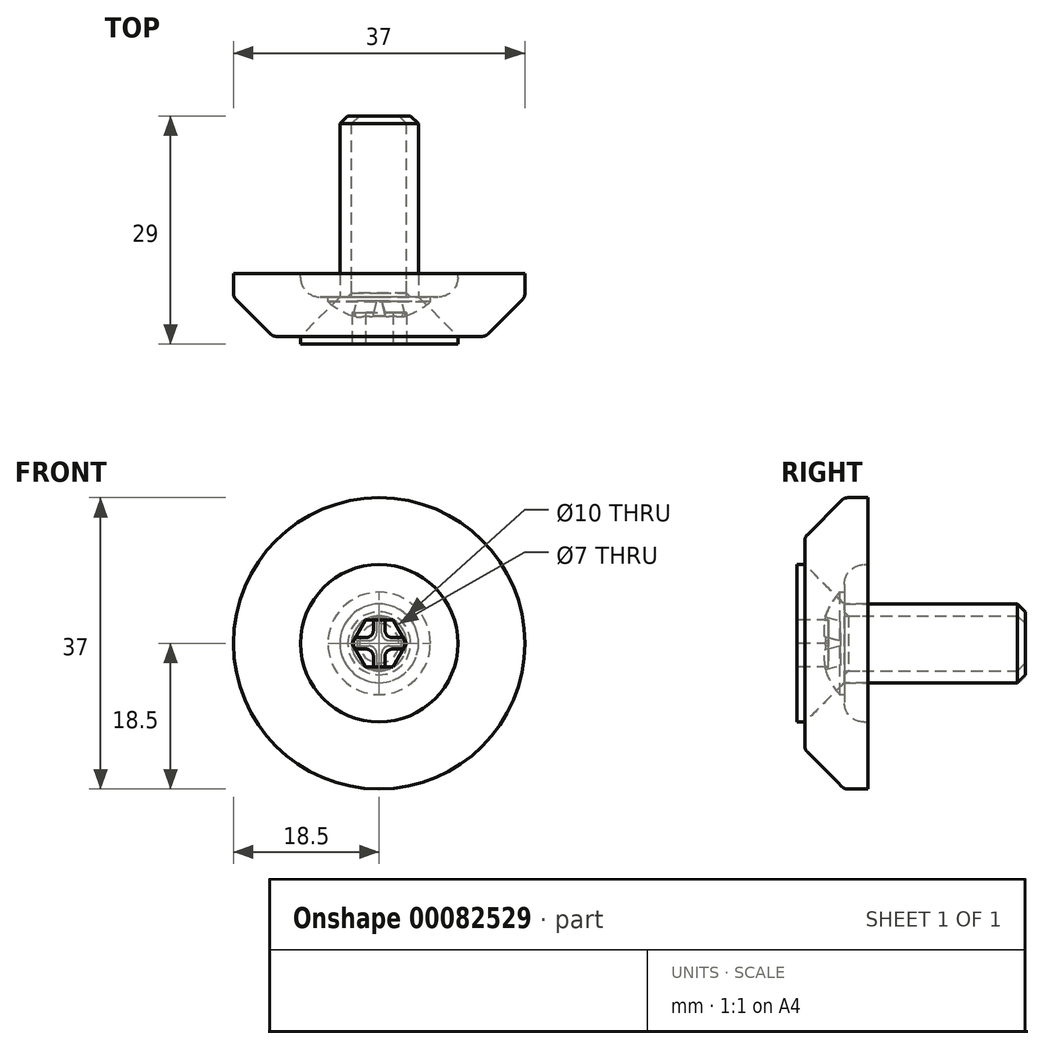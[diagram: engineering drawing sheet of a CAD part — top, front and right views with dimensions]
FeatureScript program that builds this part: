
annotation { "Feature Type Name" : "Feature", "Feature Type Description" : "" }
export const myFeature = defineFeature(function(context is Context, id is Id, definition is map)
    precondition{}
    {
        {
            var Q0;
            Q0=qCreatedBy(makeId("Top.planeOp"),FACE);
            var sketch = newSketch(context, id + "F0", { "sketchPlane" : qUnion([Q0])});
            skLineSegment(sketch, "E0", {"start": v(0, 0) * mm, "end": v(0, 50) * mm, "construction": true});
            skSolve(sketch);
        }
        {
            var Q0;
            Q0=qCreatedBy(makeId("Front.planeOp"),FACE);
            var sketch = newSketch(context, id + "F1", { "sketchPlane" : qUnion([Q0])});
            skLineSegment(sketch, "E1", {"start": v(0, 0) * mm, "end": v(0, 50) * mm, "construction": true});
            skSolve(sketch);
        }
        {
            var Q0;
            Q0=qCreatedBy(makeId("Right.planeOp"),FACE);
            var sketch = newSketch(context, id + "F2", { "sketchPlane" : qUnion([Q0])});
            skLineSegment(sketch, "E2.0", {"start": v(0, 0) * mm, "end": v(50, 0) * mm, "construction": true});
            skLineSegment(sketch, "E3", {"start": v(0, 0) * mm, "end": v(0, 10) * mm});
            skLineSegment(sketch, "E4", {"start": v(0, 10) * mm, "end": v(-0.5, 10) * mm});
            skLineSegment(sketch, "E5", {"start": v(0, 0) * mm, "end": v(-3, 0) * mm});
            skArc(sketch, "E6", {"start": v(-0.5, 10) * mm, "mid": v(-2.27, 9.27) * mm, "end": v(-3, 7.5) * mm});
            skLineSegment(sketch, "E7", {"start": v(-3, 7.5) * mm, "end": v(-3, 0) * mm});
            skSolve(sketch);
        }
        {
            var Q0;
            Q0=makeQuery(id+"F2.imprint","IMPRINT",FACE,{"disambiguationData":[TD([[makeQuery(id+"F2.imprint","IMPRINT",EDGE,{"derivedFrom":sQuery(id+"F2.wireOp",EDGE,"E3")}),1.0]])]});
            var Q1;
            Q1=sQuery(id+"F2.wireOp",EDGE,"E5");
            revolve(context, id + "F3", {"entities" : qUnion([Q0]), "axis" : qUnion([Q1]), "revolveType" : RevolveType.FULL});
        }
        {
            var Q0;
            Q0=makeQuery(id+"F3.opRevolve","SWEPT_FACE",FACE,{"disambiguationData":[OSD([sQuery(id+"F2.wireOp",EDGE,"E7")])]});
            var sketch = newSketch(context, id + "F4", { "sketchPlane" : qUnion([Q0])});
            skPoint(sketch, "E8", {"position": v(0, 0) * mm});
            skSolve(sketch);
        }
        {
            var Q0;
            Q0=sQuery(id+"F4.wireOp",VERTEX,"E8");
            var Q1;
            Q1=makeQuery(id+"F3.opRevolve","SWEPT_BODY",BODY,{"disambiguationData":[OSD([sQuery(id+"F2.wireOp",EDGE,"E3"),sQuery(id+"F2.wireOp",EDGE,"E4"),sQuery(id+"F2.wireOp",EDGE,"E5"),sQuery(id+"F2.wireOp",EDGE,"E6"),sQuery(id+"F2.wireOp",EDGE,"E7")])]});
            hole(context, id + "F5", {"style" : HoleStyle.C_SINK, "endStyle" : HoleEndStyle.THROUGH, "holeDiameter" : 7 * mm, "cSinkDiameter" : 8 * mm, "cSinkAngle" : 90 * degree, "locations" : qUnion([Q0]), "scope" : qUnion([Q1]), "isTappedThrough" : true, "startStyle" : HoleStartStyle.SKETCH});
        }
        {
            var Q0;
            Q0=qCreatedBy(makeId("Right.planeOp"),FACE);
            var sketch = newSketch(context, id + "F6", { "sketchPlane" : qUnion([Q0])});
            skLineSegment(sketch, "E9", {"start": v(0, 0) * mm, "end": v(0, 18.5) * mm});
            skLineSegment(sketch, "E10", {"start": v(0, 18.5) * mm, "end": v(-3, 18.5) * mm});
            skLineSegment(sketch, "E11", {"start": v(-3, 18.5) * mm, "end": v(-8, 13.5) * mm});
            skLineSegment(sketch, "E12", {"start": v(-8, 13.5) * mm, "end": v(-8, 0) * mm});
            skLineSegment(sketch, "E13", {"start": v(-8, 0) * mm, "end": v(0, 0) * mm});
            skLineSegment(sketch, "E14.0", {"start": v(0, 0) * mm, "end": v(50, 0) * mm, "construction": true});
            skSolve(sketch);
        }
        {
            var Q0;
            Q0=makeQuery(id+"F6.imprint","IMPRINT",FACE,{"disambiguationData":[TD([[makeQuery(id+"F6.imprint","IMPRINT",EDGE,{"derivedFrom":sQuery(id+"F6.wireOp",EDGE,"E9")}),1.0]])]});
            var Q1;
            Q1=sQuery(id+"F6.wireOp",EDGE,"E13");
            revolve(context, id + "F7", {"entities" : qUnion([Q0]), "axis" : qUnion([Q1]), "revolveType" : RevolveType.FULL});
        }
        {
            var Q0;
            Q0=makeQuery(id+"F7.opRevolve","SWEPT_FACE",FACE,{"disambiguationData":[OSD([sQuery(id+"F6.wireOp",EDGE,"E12")])]});
            var sketch = newSketch(context, id + "F8", { "sketchPlane" : qUnion([Q0])});
            skPoint(sketch, "E15", {"position": v(0, 0) * mm});
            skSolve(sketch);
        }
        {
            var Q0;
            Q0=sQuery(id+"F8.wireOp",VERTEX,"E15");
            var Q1;
            Q1=makeQuery(id+"F7.opRevolve","SWEPT_BODY",BODY,{"disambiguationData":[OSD([sQuery(id+"F6.wireOp",EDGE,"E9"),sQuery(id+"F6.wireOp",EDGE,"E10"),sQuery(id+"F6.wireOp",EDGE,"E11"),sQuery(id+"F6.wireOp",EDGE,"E12"),sQuery(id+"F6.wireOp",EDGE,"E13")])]});
            hole(context, id + "F9", {"style" : HoleStyle.C_SINK, "endStyle" : HoleEndStyle.THROUGH, "holeDiameter" : 10 * mm, "cSinkDiameter" : 20 * mm, "cSinkAngle" : 90 * degree, "locations" : qUnion([Q0]), "scope" : qUnion([Q1]), "isTappedThrough" : true, "startStyle" : HoleStartStyle.SKETCH});
        }
        {
            var Q0;
            Q0=makeQuery(id+"F7.opRevolve","SWEPT_FACE",FACE,{"disambiguationData":[OSD([sQuery(id+"F6.wireOp",EDGE,"E11")])]});
            fillet(context, id + "F10", {"entities" : qUnion([Q0]), "radius" : 1 * mm, "tangentPropagation" : true, "allowEdgeOverflow" : false});
        }
        {
            var Q0;
            Q0=qCreatedBy(makeId("Front.planeOp"),FACE);
            cPlane(context, id + "F11", {"entities" : qUnion([Q0]), "cplaneType" : CPlaneType.OFFSET, "offset" : 20 * mm, "oppositeDirection" : true, "width" : 150 * mm, "height" : 150 * mm});
        }
        {
            var Q0;
            Q0=qCreatedBy(makeId("Right.planeOp"),FACE);
            var sketch = newSketch(context, id + "F12", { "sketchPlane" : qUnion([Q0])});
            skLineSegment(sketch, "E16", {"start": v(20, 3.5) * mm, "end": v(-3, 3.5) * mm});
            skLineSegment(sketch, "E17", {"start": v(-3, 3.5) * mm, "end": v(-3, 6.5) * mm});
            skLineSegment(sketch, "E18", {"start": v(-3, 6.5) * mm, "end": v(-3.6, 6.5) * mm});
            skLineSegment(sketch, "E19", {"start": v(20, 3.5) * mm, "end": v(20, 0) * mm});
            skLineSegment(sketch, "E20", {"start": v(20, 0) * mm, "end": v(-6, 0) * mm});
            skArc(sketch, "E21", {"start": v(-3.6, 6.5) * mm, "mid": v(-5.38, 3.46) * mm, "end": v(-6, 0) * mm});
            skLineSegment(sketch, "E22", {"start": v(-2.5, 3.5) * mm, "end": v(0, 3.5) * mm, "construction": true});
            skLineSegment(sketch, "E23.0", {"start": v(0, 0) * mm, "end": v(50, 0) * mm, "construction": true});
            skSolve(sketch);
        }
        {
            var Q0;
            Q0 = qSketchRegion(id + "F12", true);
            var Q1;
            Q1=sQuery(id+"F12.wireOp",EDGE,"E20");
            revolve(context, id + "F13", {"entities" : qUnion([Q0]), "axis" : qUnion([Q1]), "revolveType" : RevolveType.FULL});
        }
        {
            var Q0;
            Q0=qCreatedBy(makeId("Front.planeOp"),FACE);
            var Q1;
            Q1=sQuery(id+"F12.wireOp",VERTEX,"E21.end");
            cPlane(context, id + "F14", {"entities" : qUnion([Q0, Q1]), "cplaneType" : CPlaneType.PLANE_POINT, "offset" : 150 * mm, "width" : 150 * mm, "height" : 150 * mm});
        }
        {
            var Q0;
            Q0=qCreatedBy(id+"F14.planeOp",FACE);
            var sketch = newSketch(context, id + "F15", { "sketchPlane" : qUnion([Q0])});
            skLineSegment(sketch, "E24.bottom", {"start": v(1, 3.5) * mm, "end": v(-1, 3.5) * mm});
            skLineSegment(sketch, "E24.top", {"start": v(1, -3.5) * mm, "end": v(-1, -3.5) * mm});
            skLineSegment(sketch, "E24.left", {"start": v(1, 3.5) * mm, "end": v(1, -3.5) * mm});
            skLineSegment(sketch, "E24.right", {"start": v(-1, 3.5) * mm, "end": v(-1, -3.5) * mm});
            skPoint(sketch, "E24.middle", {"position": v(0, 0) * mm});
            skLineSegment(sketch, "E25.bottom", {"start": v(3.5, -1) * mm, "end": v(-3.5, -1) * mm});
            skLineSegment(sketch, "E25.top", {"start": v(3.5, 1) * mm, "end": v(-3.5, 1) * mm});
            skLineSegment(sketch, "E25.left", {"start": v(3.5, -1) * mm, "end": v(3.5, 1) * mm});
            skLineSegment(sketch, "E25.right", {"start": v(-3.5, -1) * mm, "end": v(-3.5, 1) * mm});
            skSolve(sketch);
        }
        {
            var Q0;
            Q0 = qSketchRegion(id + "F15", true);
            extrude(context, id + "F16", {"entities" : qUnion([Q0]), "operationType" : NewBodyOperationType.REMOVE, "oppositeDirection" : true, "depth" : 2.5 * mm, "hasDraft" : true, "draftAngle" : 15 * degree, "draftPullDirection" : true});
        }
        {
            var Q0;
            Q0=makeQuery(id+"F16.boolean.opBoolean","COPY",EDGE,{"derivedFrom":makeQuery(id+"F16.opExtrude","SWEPT_EDGE",EDGE,{"disambiguationData":[OSD([sQuery(id+"F15.wireOp",EDGE,"E24.right"),sQuery(id+"F15.wireOp",EDGE,"E25.top")])]})});
            var Q1;
            Q1=makeQuery(id+"F16.boolean.opBoolean","COPY",EDGE,{"derivedFrom":makeQuery(id+"F16.opExtrude","SWEPT_EDGE",EDGE,{"disambiguationData":[OSD([sQuery(id+"F15.wireOp",EDGE,"E24.left"),sQuery(id+"F15.wireOp",EDGE,"E25.top")])]})});
            var Q2;
            Q2=makeQuery(id+"F16.boolean.opBoolean","COPY",EDGE,{"derivedFrom":makeQuery(id+"F16.opExtrude","SWEPT_EDGE",EDGE,{"disambiguationData":[OSD([sQuery(id+"F15.wireOp",EDGE,"E24.left"),sQuery(id+"F15.wireOp",EDGE,"E25.bottom")])]})});
            var Q3;
            Q3=makeQuery(id+"F16.boolean.opBoolean","COPY",EDGE,{"derivedFrom":makeQuery(id+"F16.opExtrude","SWEPT_EDGE",EDGE,{"disambiguationData":[OSD([sQuery(id+"F15.wireOp",EDGE,"E24.right"),sQuery(id+"F15.wireOp",EDGE,"E25.bottom")])]})});
            fillet(context, id + "F17", {"entities" : qUnion([Q0, Q1, Q2, Q3]), "radius" : 1 * mm, "tangentPropagation" : true, "allowEdgeOverflow" : false});
        }
        {
            var Q0;
            Q0=qCreatedBy(makeId("Right.planeOp"),FACE);
            var sketch = newSketch(context, id + "F18", { "sketchPlane" : qUnion([Q0])});
            skLineSegment(sketch, "E26", {"start": v(20, 5) * mm, "end": v(-3, 5) * mm});
            skLineSegment(sketch, "E27", {"start": v(-3, 5) * mm, "end": v(-8, 10) * mm});
            skLineSegment(sketch, "E28", {"start": v(-8, 10) * mm, "end": v(-9, 10) * mm});
            skLineSegment(sketch, "E29", {"start": v(-9, 10) * mm, "end": v(-9, 0) * mm});
            skLineSegment(sketch, "E30", {"start": v(-9, 0) * mm, "end": v(20, 0) * mm});
            skLineSegment(sketch, "E31", {"start": v(20, 0) * mm, "end": v(20, 5) * mm});
            skLineSegment(sketch, "E32", {"start": v(-3, 5) * mm, "end": v(0, 5) * mm, "construction": true});
            skLineSegment(sketch, "E33.0", {"start": v(0, 0) * mm, "end": v(50, 0) * mm, "construction": true});
            skSolve(sketch);
        }
        {
            var Q0;
            Q0=makeQuery(id+"F18.imprint","IMPRINT",FACE,{"disambiguationData":[TD([[makeQuery(id+"F18.imprint","IMPRINT",EDGE,{"derivedFrom":sQuery(id+"F18.wireOp",EDGE,"E26")}),1.0]])]});
            var Q1;
            Q1=sQuery(id+"F18.wireOp",EDGE,"E30");
            revolve(context, id + "F19", {"entities" : qUnion([Q0]), "axis" : qUnion([Q1]), "revolveType" : RevolveType.FULL});
        }
        {
            var Q0;
            Q0=makeQuery(id+"F19.opRevolve","SWEPT_FACE",FACE,{"disambiguationData":[OSD([sQuery(id+"F18.wireOp",EDGE,"E29")])]});
            var sketch = newSketch(context, id + "F20", { "sketchPlane" : qUnion([Q0])});
            skCircle(sketch, "E34.cCircle", {"center": v(0, 0) * mm, "radius": 3 * mm, "construction": true});
            skLineSegment(sketch, "E34.0", {"start": v(-1.73, 3) * mm, "end": v(1.73, 3) * mm});
            skLineSegment(sketch, "E34.1", {"start": v(1.73, 3) * mm, "end": v(3.46, 0) * mm});
            skLineSegment(sketch, "E34.2", {"start": v(3.46, 0) * mm, "end": v(1.73, -3) * mm});
            skLineSegment(sketch, "E34.3", {"start": v(1.73, -3) * mm, "end": v(-1.73, -3) * mm});
            skLineSegment(sketch, "E34.4", {"start": v(-1.73, -3) * mm, "end": v(-3.46, 0) * mm});
            skLineSegment(sketch, "E34.5", {"start": v(-3.46, 0) * mm, "end": v(-1.73, 3) * mm});
            skPoint(sketch, "E34.0.midPoint", {"position": v(0, 3) * mm});
            skSolve(sketch);
        }
        {
            var Q0;
            Q0 = qSketchRegion(id + "F20", true);
            extrude(context, id + "F21", {"entities" : qUnion([Q0]), "operationType" : NewBodyOperationType.REMOVE, "oppositeDirection" : true, "depth" : 4 * mm});
        }
        {
            var Q0;
            Q0=makeQuery(id+"F13.opRevolve","SWEPT_EDGE",EDGE,{"disambiguationData":[OSD([sQuery(id+"F12.wireOp",EDGE,"E16"),sQuery(id+"F12.wireOp",EDGE,"E19")])]});
            var Q1;
            Q1=makeQuery(id+"F19.opRevolve","SWEPT_EDGE",EDGE,{"disambiguationData":[OSD([sQuery(id+"F18.wireOp",EDGE,"E26"),sQuery(id+"F18.wireOp",EDGE,"E31")])]});
            chamfer(context, id + "F22", {"entities" : qUnion([Q0, Q1]), "width" : 1 * mm, "tangentPropagation" : true});
        }
    });
